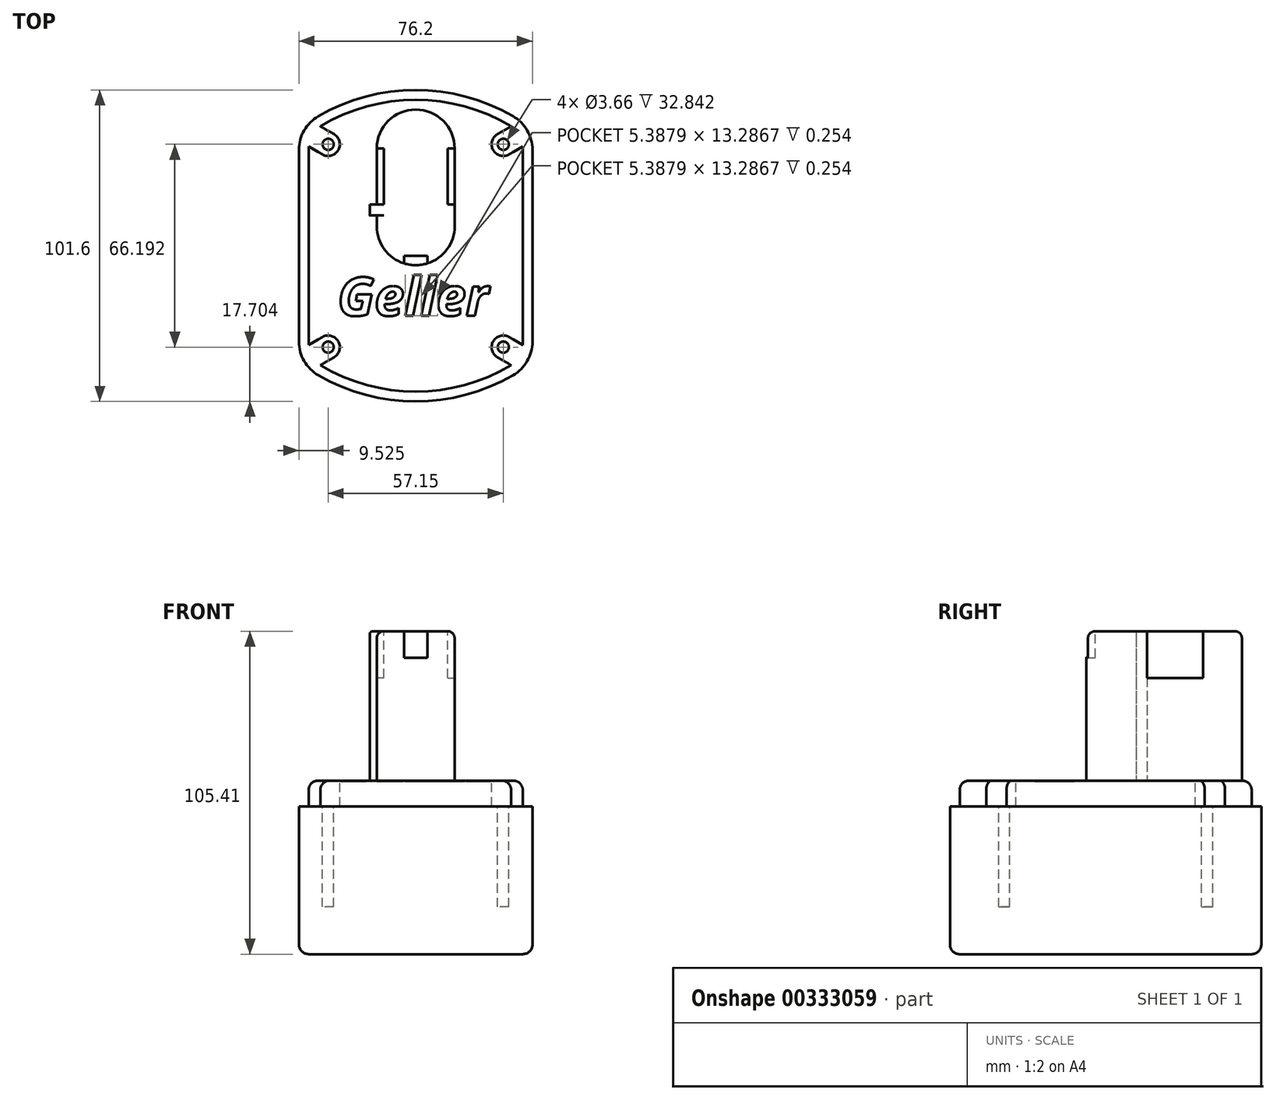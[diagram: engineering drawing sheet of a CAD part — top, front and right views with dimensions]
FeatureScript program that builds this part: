
annotation { "Feature Type Name" : "Feature", "Feature Type Description" : "" }
export const myFeature = defineFeature(function(context is Context, id is Id, definition is map)
    precondition{}
    {
        {
            var Q0;
            Q0=qCreatedBy(makeId("Top.planeOp"),FACE);
            var sketch = newSketch(context, id + "F0", { "sketchPlane" : qUnion([Q0])});
            skLineSegment(sketch, "E0.bottom", {"start": v(38.1, 38.1) * mm, "end": v(-38.1, 38.1) * mm, "construction": true});
            skLineSegment(sketch, "E0.top", {"start": v(38.1, -38.1) * mm, "end": v(-38.1, -38.1) * mm, "construction": true});
            skLineSegment(sketch, "E0.left", {"start": v(38.1, 38.1) * mm, "end": v(38.1, -38.1) * mm});
            skLineSegment(sketch, "E0.right", {"start": v(-38.1, 38.1) * mm, "end": v(-38.1, -38.1) * mm});
            skPoint(sketch, "E0.middle", {"position": v(0, 0) * mm});
            skLineSegment(sketch, "E1", {"start": v(0, 38.1) * mm, "end": v(0, 50.8) * mm, "construction": true});
            skPoint(sketch, "E1.endSnap0", {"position": v(0, 38.1) * mm});
            skArc(sketch, "E2", {"start": v(38.1, 38.1) * mm, "mid": v(0, 50.8) * mm, "end": v(-38.1, 38.1) * mm});
            skLineSegment(sketch, "E3", {"start": v(-38.1, 0) * mm, "end": v(38.1, 0) * mm, "construction": true});
            skArc(sketch, "E4.MirrorCS", {"start": v(38.1, -38.1) * mm, "mid": v(0, -50.8) * mm, "end": v(-38.1, -38.1) * mm});
            skSolve(sketch);
        }
        {
            var Q0;
            Q0 = qSketchRegion(id + "F0", true);
            extrude(context, id + "F1", {"entities" : qUnion([Q0]), "oppositeDirection" : true, "depth" : 48.26 * mm});
        }
        {
            var Q0;
            Q0=makeQuery(id+"F1.opExtrude","CAP_FACE",FACE,{"disambiguationData":[OSD([sQuery(id+"F0.wireOp",EDGE,"E0.left"),sQuery(id+"F0.wireOp",EDGE,"E0.right"),sQuery(id+"F0.wireOp",EDGE,"E2"),sQuery(id+"F0.wireOp",EDGE,"E4.MirrorCS")])],"isStart":true});
            var sketch = newSketch(context, id + "F2", { "sketchPlane" : qUnion([Q0])});
            skArc(sketch, "E5.0.0", {"start": v(38.1, 38.1) * mm, "mid": v(0, 50.8) * mm, "end": v(-38.1, 38.1) * mm, "construction": true});
            skLineSegment(sketch, "E5.0.1", {"start": v(-38.1, 38.1) * mm, "end": v(-38.1, -38.1) * mm, "construction": true});
            skArc(sketch, "E5.0.2", {"start": v(-38.1, -38.1) * mm, "mid": v(0, -50.8) * mm, "end": v(38.1, -38.1) * mm, "construction": true});
            skLineSegment(sketch, "E5.0.3", {"start": v(38.1, -38.1) * mm, "end": v(38.1, 38.1) * mm, "construction": true});
            skArc(sketch, "E6.0", {"start": v(34.93, 36.49) * mm, "mid": v(0, 47.63) * mm, "end": v(-34.93, 36.49) * mm});
            skLineSegment(sketch, "E6.1", {"start": v(34.93, -36.49) * mm, "end": v(34.93, 36.49) * mm});
            skArc(sketch, "E6.2", {"start": v(-34.93, -36.49) * mm, "mid": v(0, -47.63) * mm, "end": v(34.93, -36.49) * mm});
            skLineSegment(sketch, "E6.3", {"start": v(-34.93, 36.49) * mm, "end": v(-34.93, -36.49) * mm});
            skSolve(sketch);
        }
        {
            var Q0;
            Q0 = qSketchRegion(id + "F2", true);
            extrude(context, id + "F3", {"entities" : qUnion([Q0]), "operationType" : NewBodyOperationType.ADD, "depth" : 8.38 * mm});
        }
        {
            var Q0;
            Q0=makeQuery(id+"F3.opExtrude","CAP_FACE",FACE,{"disambiguationData":[OSD([sQuery(id+"F2.wireOp",EDGE,"E6.0"),sQuery(id+"F2.wireOp",EDGE,"E6.1"),sQuery(id+"F2.wireOp",EDGE,"E6.2"),sQuery(id+"F2.wireOp",EDGE,"E6.3")])],"isStart":false});
            var sketch = newSketch(context, id + "F4", { "sketchPlane" : qUnion([Q0])});
            skLineSegment(sketch, "E7.bottom", {"start": v(28.58, 33.1) * mm, "end": v(-28.58, 33.1) * mm, "construction": true});
            skLineSegment(sketch, "E7.top", {"start": v(28.57, -33.1) * mm, "end": v(-28.58, -33.1) * mm, "construction": true});
            skLineSegment(sketch, "E7.left", {"start": v(28.58, 33.1) * mm, "end": v(28.57, -33.1) * mm, "construction": true});
            skLineSegment(sketch, "E7.right", {"start": v(-28.58, 33.1) * mm, "end": v(-28.58, -33.1) * mm, "construction": true});
            skPoint(sketch, "E7.middle", {"position": v(0, 0) * mm});
            skLineSegment(sketch, "E8", {"start": v(-28.58, -33.1) * mm, "end": v(-50.57, -45.8) * mm, "construction": true});
            skArc(sketch, "E9.0.startCap", {"start": v(-30.48, -29.8) * mm, "mid": v(-25.28, -31.2) * mm, "end": v(-26.67, -36.4) * mm});
            skArc(sketch, "E9.0.endCap", {"start": v(-48.67, -49.1) * mm, "mid": v(-53.87, -47.7) * mm, "end": v(-52.48, -42.5) * mm});
            skLineSegment(sketch, "E9.0.left", {"start": v(-26.67, -36.4) * mm, "end": v(-48.67, -49.1) * mm});
            skLineSegment(sketch, "E9.0.right", {"start": v(-30.48, -29.8) * mm, "end": v(-52.48, -42.5) * mm});
            skLineSegment(sketch, "E10", {"start": v(-28.58, 0) * mm, "end": v(28.58, 0) * mm, "construction": true});
            skLineSegment(sketch, "E11", {"start": v(0, 33.1) * mm, "end": v(0, -33.1) * mm, "construction": true});
            skArc(sketch, "E12.MirrorCS", {"start": v(30.48, -29.8) * mm, "mid": v(25.28, -31.2) * mm, "end": v(26.67, -36.4) * mm});
            skLineSegment(sketch, "E13.MirrorCS", {"start": v(26.67, -36.4) * mm, "end": v(48.67, -49.1) * mm});
            skLineSegment(sketch, "E14.MirrorCS", {"start": v(30.48, -29.8) * mm, "end": v(52.48, -42.5) * mm});
            skArc(sketch, "E15.MirrorCS", {"start": v(48.67, -49.1) * mm, "mid": v(53.87, -47.7) * mm, "end": v(52.48, -42.5) * mm});
            skLineSegment(sketch, "E16.MirrorCS", {"start": v(30.48, 29.8) * mm, "end": v(52.48, 42.5) * mm});
            skLineSegment(sketch, "E17.MirrorCS", {"start": v(26.67, 36.4) * mm, "end": v(48.67, 49.1) * mm});
            skArc(sketch, "E18.MirrorCS", {"start": v(30.48, 29.8) * mm, "mid": v(25.28, 31.2) * mm, "end": v(26.67, 36.4) * mm});
            skArc(sketch, "E19.MirrorCS", {"start": v(48.67, 49.1) * mm, "mid": v(53.87, 47.7) * mm, "end": v(52.48, 42.5) * mm});
            skArc(sketch, "E20.MirrorCS", {"start": v(-30.48, 29.8) * mm, "mid": v(-25.28, 31.2) * mm, "end": v(-26.67, 36.4) * mm});
            skLineSegment(sketch, "E21.MirrorCS", {"start": v(-26.67, 36.4) * mm, "end": v(-48.67, 49.1) * mm});
            skLineSegment(sketch, "E22.MirrorCS", {"start": v(-30.48, 29.8) * mm, "end": v(-52.48, 42.5) * mm});
            skArc(sketch, "E23.MirrorCS", {"start": v(-48.67, 49.1) * mm, "mid": v(-53.87, 47.7) * mm, "end": v(-52.48, 42.5) * mm});
            skCircle(sketch, "E24", {"center": v(-28.58, 33.1) * mm, "radius": 1.83 * mm, "construction": true});
            skCircle(sketch, "E25", {"center": v(28.58, 33.1) * mm, "radius": 1.83 * mm, "construction": true});
            skCircle(sketch, "E26", {"center": v(-28.58, -33.1) * mm, "radius": 1.83 * mm, "construction": true});
            skCircle(sketch, "E27", {"center": v(28.57, -33.1) * mm, "radius": 1.83 * mm, "construction": true});
            skSolve(sketch);
        }
        {
            var Q0;
            Q0 = qSketchRegion(id + "F4", true);
            var Q1;
            Q1=makeQuery(id+"F1.opExtrude","CAP_FACE",FACE,{"disambiguationData":[OSD([sQuery(id+"F0.wireOp",EDGE,"E0.left"),sQuery(id+"F0.wireOp",EDGE,"E0.right"),sQuery(id+"F0.wireOp",EDGE,"E2"),sQuery(id+"F0.wireOp",EDGE,"E4.MirrorCS")])],"isStart":true});
            extrude(context, id + "F5", {"entities" : qUnion([Q0]), "operationType" : NewBodyOperationType.REMOVE, "endBound" : BoundingType.UP_TO_SURFACE, "oppositeDirection" : true, "endBoundEntityFace" : qUnion([Q1]), "depth" : 25.4 * mm});
        }
        {
            var Q0;
            Q0=makeQuery(id+"F2.imprint","IMPRINT",FACE,{"disambiguationData":[TD([[makeQuery(id+"F2.imprint","IMPRINT",EDGE,{"derivedFrom":sQuery(id+"F2.wireOp",EDGE,"E6.0")}),-1.0]])]});
            var sketch = newSketch(context, id + "F6", { "sketchPlane" : qUnion([Q0])});
            skCircle(sketch, "E28.0", {"center": v(-28.58, 33.1) * mm, "radius": 1.83 * mm});
            skCircle(sketch, "E28.1", {"center": v(28.58, 33.1) * mm, "radius": 1.83 * mm});
            skCircle(sketch, "E28.2", {"center": v(28.57, -33.1) * mm, "radius": 1.83 * mm});
            skCircle(sketch, "E28.3", {"center": v(-28.58, -33.1) * mm, "radius": 1.83 * mm});
            skSolve(sketch);
        }
        {
            var Q0;
            Q0 = qSketchRegion(id + "F6", true);
            extrude(context, id + "F7", {"entities" : qUnion([Q0]), "operationType" : NewBodyOperationType.REMOVE, "oppositeDirection" : true, "depth" : 32.84 * mm});
        }
        {
            var Q0;
            Q0=qCreatedBy(makeId("Top.planeOp"),FACE);
            var sketch = newSketch(context, id + "F8", { "sketchPlane" : qUnion([Q0])});
            skLineSegment(sketch, "E29", {"start": v(0, 6.35) * mm, "end": v(0, 31.75) * mm, "construction": true});
            skArc(sketch, "E30.0.startCap", {"start": v(12.7, 6.35) * mm, "mid": v(0, -6.35) * mm, "end": v(-12.7, 6.35) * mm});
            skArc(sketch, "E30.0.endCap", {"start": v(-12.7, 31.75) * mm, "mid": v(0, 44.45) * mm, "end": v(12.7, 31.75) * mm});
            skLineSegment(sketch, "E30.0.left", {"start": v(-12.7, 6.35) * mm, "end": v(-12.7, 31.75) * mm});
            skLineSegment(sketch, "E30.0.right", {"start": v(12.7, 6.35) * mm, "end": v(12.7, 31.75) * mm});
            skPoint(sketch, "E31", {"position": v(0, 19.05) * mm});
            skPoint(sketch, "E32", {"position": v(0, 44.45) * mm});
            skPoint(sketch, "E33", {"position": v(0, -6.35) * mm});
            skSolve(sketch);
        }
        {
            var Q0;
            Q0 = qSketchRegion(id + "F8", true);
            extrude(context, id + "F9", {"entities" : qUnion([Q0]), "operationType" : NewBodyOperationType.ADD, "depth" : 57.15 * mm});
        }
        {
            var Q0;
            Q0=makeQuery(id+"F3.opExtrude","CAP_FACE",FACE,{"disambiguationData":[OSD([sQuery(id+"F2.wireOp",EDGE,"E6.0"),sQuery(id+"F2.wireOp",EDGE,"E6.1"),sQuery(id+"F2.wireOp",EDGE,"E6.2"),sQuery(id+"F2.wireOp",EDGE,"E6.3")])],"isStart":false});
            var sketch = newSketch(context, id + "F10", { "sketchPlane" : qUnion([Q0])});
            skLineSegment(sketch, "E34.bottom", {"start": v(-12.7, 13.46) * mm, "end": v(-14.99, 13.46) * mm});
            skLineSegment(sketch, "E34.top", {"start": v(-12.7, 9.9) * mm, "end": v(-14.99, 9.9) * mm});
            skLineSegment(sketch, "E34.left", {"start": v(-12.7, 13.46) * mm, "end": v(-12.7, 9.9) * mm});
            skLineSegment(sketch, "E34.right", {"start": v(-14.99, 13.46) * mm, "end": v(-14.99, 9.9) * mm});
            skSolve(sketch);
        }
        {
            var Q0;
            Q0 = qSketchRegion(id + "F10", true);
            var Q1;
            Q1=makeQuery(id+"F9.opExtrude","CAP_FACE",FACE,{"disambiguationData":[OSD([sQuery(id+"F8.wireOp",EDGE,"E30.0.startCap"),sQuery(id+"F8.wireOp",EDGE,"E30.0.endCap"),sQuery(id+"F8.wireOp",EDGE,"E30.0.left"),sQuery(id+"F8.wireOp",EDGE,"E30.0.right")])],"isStart":false});
            extrude(context, id + "F11", {"entities" : qUnion([Q0]), "operationType" : NewBodyOperationType.ADD, "endBound" : BoundingType.UP_TO_SURFACE, "endBoundEntityFace" : qUnion([Q1]), "depth" : 25.4 * mm});
        }
        {
            var Q0;
            Q0=makeQuery(id+"F9.opExtrude","CAP_EDGE",EDGE,{"disambiguationData":[OSD([sQuery(id+"F8.wireOp",EDGE,"E30.0.right")])],"isStart":false});
            fillet(context, id + "F12", {"entities" : qUnion([Q0]), "radius" : 2.3 * mm, "tangentPropagation" : true, "allowEdgeOverflow" : false});
        }
        {
            var Q0;
            Q0=makeQuery(id+"F11.boolean.opBoolean","MERGE",FACE,{"derivedFrom":[makeQuery(id+"F9.opExtrude","CAP_FACE",FACE,{"disambiguationData":[OSD([sQuery(id+"F8.wireOp",EDGE,"E30.0.startCap"),sQuery(id+"F8.wireOp",EDGE,"E30.0.endCap"),sQuery(id+"F8.wireOp",EDGE,"E30.0.left"),sQuery(id+"F8.wireOp",EDGE,"E30.0.right")])],"isStart":false}),makeQuery(id+"F11.opExtrude","CAP_FACE",FACE,{"disambiguationData":[OSD([sQuery(id+"F10.wireOp",EDGE,"E34.bottom"),sQuery(id+"F10.wireOp",EDGE,"E34.top"),sQuery(id+"F10.wireOp",EDGE,"E34.left"),sQuery(id+"F10.wireOp",EDGE,"E34.right")])],"isStart":false})]});
            var sketch = newSketch(context, id + "F13", { "sketchPlane" : qUnion([Q0])});
            skLineSegment(sketch, "E35.bottom", {"start": v(10.41, 31.75) * mm, "end": v(12.7, 31.75) * mm});
            skLineSegment(sketch, "E35.top", {"start": v(10.41, 13.46) * mm, "end": v(12.7, 13.46) * mm});
            skLineSegment(sketch, "E35.left", {"start": v(10.41, 31.75) * mm, "end": v(10.41, 13.46) * mm});
            skLineSegment(sketch, "E35.right", {"start": v(12.7, 31.75) * mm, "end": v(12.7, 13.46) * mm});
            skLineSegment(sketch, "E36.0", {"start": v(0, 6.35) * mm, "end": v(0, 31.75) * mm, "construction": true});
            skLineSegment(sketch, "E37.MirrorCS", {"start": v(-10.41, 31.75) * mm, "end": v(-12.7, 31.75) * mm});
            skLineSegment(sketch, "E38.MirrorCS", {"start": v(-12.7, 31.75) * mm, "end": v(-12.7, 13.46) * mm});
            skLineSegment(sketch, "E39.MirrorCS", {"start": v(-10.41, 31.75) * mm, "end": v(-10.41, 13.46) * mm});
            skLineSegment(sketch, "E40.MirrorCS", {"start": v(-10.41, 13.46) * mm, "end": v(-12.7, 13.46) * mm});
            skArc(sketch, "E41.0", {"start": v(3.81, -5.77) * mm, "mid": v(0, -6.35) * mm, "end": v(-3.81, -5.77) * mm, "construction": true});
            skArc(sketch, "E41.1", {"start": v(-10.41, 6.35) * mm, "mid": v(0, -4.06) * mm, "end": v(10.41, 6.35) * mm, "construction": true});
            skLineSegment(sketch, "E42", {"start": v(-3.8, -5.77) * mm, "end": v(-3.8, -3.34) * mm, "construction": true});
            skLineSegment(sketch, "E43", {"start": v(-3.8, -3.34) * mm, "end": v(3.8, -3.34) * mm, "construction": true});
            skLineSegment(sketch, "E44", {"start": v(3.81, -3.34) * mm, "end": v(3.81, -5.77) * mm, "construction": true});
            skPoint(sketch, "E45.orphan", {"position": v(-12.7, 6.35) * mm});
            skPoint(sketch, "E46.orphan", {"position": v(12.7, 6.35) * mm});
            skSolve(sketch);
        }
        {
            var Q0;
            Q0 = qSketchRegion(id + "F13", true);
            extrude(context, id + "F14", {"entities" : qUnion([Q0]), "operationType" : NewBodyOperationType.REMOVE, "oppositeDirection" : true, "depth" : 15.24 * mm});
        }
        {
            var Q0;
            {var subQ7=sQuery(id+"F13.wireOp",EDGE,"E35.left");Q0=makeQuery(id+"F13.imprint","IMPRINT",FACE,{"disambiguationData":[TD([[makeQuery(id+"F13.imprint","IMPRINT",EDGE,{"derivedFrom":subQ7}),1.0]])]});}
            var sketch = newSketch(context, id + "F15", { "sketchPlane" : qUnion([Q0])});
            skLineSegment(sketch, "E47.0", {"start": v(-3.8, -5.77) * mm, "end": v(-3.8, -3.34) * mm});
            skLineSegment(sketch, "E47.1", {"start": v(-3.8, -3.34) * mm, "end": v(3.8, -3.34) * mm});
            skLineSegment(sketch, "E47.2", {"start": v(3.81, -3.34) * mm, "end": v(3.81, -5.77) * mm});
            skArc(sketch, "E48.0", {"start": v(3.8, -5.77) * mm, "mid": v(0, -6.35) * mm, "end": v(-3.81, -5.77) * mm});
            skPoint(sketch, "E49.orphan", {"position": v(-12.7, 6.35) * mm});
            skPoint(sketch, "E50.orphan", {"position": v(12.7, 6.35) * mm});
            skSolve(sketch);
        }
        {
            var Q0;
            Q0 = qSketchRegion(id + "F15", true);
            extrude(context, id + "F16", {"entities" : qUnion([Q0]), "operationType" : NewBodyOperationType.REMOVE, "oppositeDirection" : true, "depth" : 8.64 * mm});
        }
        {
            var Q0;
            Q0=makeQuery(id+"F11.opExtrude","CAP_EDGE",EDGE,{"disambiguationData":[OSD([sQuery(id+"F10.wireOp",EDGE,"E34.right")])],"isStart":false});
            fillet(context, id + "F17", {"entities" : qUnion([Q0]), "radius" : 1.02 * mm, "tangentPropagation" : true, "allowEdgeOverflow" : false});
        }
        {
            var Q0;
            Q0=makeQuery(id+"F3.opExtrude","CAP_FACE",FACE,{"disambiguationData":[OSD([sQuery(id+"F2.wireOp",EDGE,"E6.0"),sQuery(id+"F2.wireOp",EDGE,"E6.1"),sQuery(id+"F2.wireOp",EDGE,"E6.2"),sQuery(id+"F2.wireOp",EDGE,"E6.3")])],"isStart":false});
            var sketch = newSketch(context, id + "F18", { "sketchPlane" : qUnion([Q0])});
            skText(sketch, "E51", { "text": "Geller", "fontName": "OpenSans-BoldItalic.ttf"});
            skArc(sketch, "E52.0", {"start": v(-38.1, -38.1) * mm, "mid": v(0, -50.8) * mm, "end": v(38.1, -38.1) * mm});
            skLineSegment(sketch, "E53", {"start": v(0, -50.8) * mm, "end": v(0, -22.86) * mm, "construction": true});
            const initialGuessF18  = {"E51": [-0.02554, -0.02286, 1, 0, 0.01259]};
            skSetInitialGuess(sketch, initialGuessF18);
            skSolve(sketch);
        }
        {
            var Q0;
            Q0=makeQuery(id+"F18.imprint","IMPRINT",FACE,{"disambiguationData":[TD([[makeQuery(id+"F18.imprint","IMPRINT",EDGE,{"derivedFrom":sQuery(id+"F18.wireOp",EDGE,"E51.sketch_text.stroke-22")}),-1.0]])]});
            var Q1;
            Q1=makeQuery(id+"F18.imprint","IMPRINT",FACE,{"disambiguationData":[TD([[makeQuery(id+"F18.imprint","IMPRINT",EDGE,{"derivedFrom":sQuery(id+"F18.wireOp",EDGE,"E51.sketch_text.stroke-0")}),-1.0]])]});
            var Q2;
            Q2=makeQuery(id+"F18.imprint","IMPRINT",FACE,{"disambiguationData":[TD([[makeQuery(id+"F18.imprint","IMPRINT",EDGE,{"derivedFrom":sQuery(id+"F18.wireOp",EDGE,"E51.sketch_text.stroke-46")}),-1.0]])]});
            var Q3;
            Q3=makeQuery(id+"F18.imprint","IMPRINT",FACE,{"disambiguationData":[TD([[makeQuery(id+"F18.imprint","IMPRINT",EDGE,{"derivedFrom":sQuery(id+"F18.wireOp",EDGE,"E51.sketch_text.stroke-50")}),-1.0]])]});
            var Q4;
            Q4=makeQuery(id+"F18.imprint","IMPRINT",FACE,{"disambiguationData":[TD([[makeQuery(id+"F18.imprint","IMPRINT",EDGE,{"derivedFrom":sQuery(id+"F18.wireOp",EDGE,"E51.sketch_text.stroke-54")}),-1.0]])]});
            var Q5;
            Q5=makeQuery(id+"F18.imprint","IMPRINT",FACE,{"disambiguationData":[TD([[makeQuery(id+"F18.imprint","IMPRINT",EDGE,{"derivedFrom":sQuery(id+"F18.wireOp",EDGE,"E51.sketch_text.stroke-78")}),-1.0]])]});
            extrude(context, id + "F19", {"entities" : qUnion([Q0, Q1, Q2, Q3, Q4, Q5]), "operationType" : NewBodyOperationType.REMOVE, "oppositeDirection" : true, "depth" : 0.25 * mm});
        }
        {
            var Q0;
            Q0=makeQuery(id+"F1.opExtrude","SWEPT_EDGE",EDGE,{"disambiguationData":[OSD([sQuery(id+"F0.wireOp",EDGE,"E0.left"),sQuery(id+"F0.wireOp",EDGE,"E4.MirrorCS")])]});
            var Q1;
            Q1=makeQuery(id+"F1.opExtrude","SWEPT_EDGE",EDGE,{"disambiguationData":[OSD([sQuery(id+"F0.wireOp",EDGE,"E0.left"),sQuery(id+"F0.wireOp",EDGE,"E2")])]});
            var Q2;
            Q2=makeQuery(id+"F1.opExtrude","SWEPT_EDGE",EDGE,{"disambiguationData":[OSD([sQuery(id+"F0.wireOp",EDGE,"E0.right"),sQuery(id+"F0.wireOp",EDGE,"E4.MirrorCS")])]});
            var Q3;
            Q3=makeQuery(id+"F1.opExtrude","SWEPT_EDGE",EDGE,{"disambiguationData":[OSD([sQuery(id+"F0.wireOp",EDGE,"E0.right"),sQuery(id+"F0.wireOp",EDGE,"E2")])]});
            fillet(context, id + "F20", {"entities" : qUnion([Q0, Q1, Q2, Q3]), "radius" : 12.7 * mm, "tangentPropagation" : true, "allowEdgeOverflow" : false});
        }
        {
            var Q0;
            Q0=makeQuery(id+"F3.opExtrude","CAP_EDGE",EDGE,{"disambiguationData":[OSD([sQuery(id+"F2.wireOp",EDGE,"E6.2")])],"isStart":false});
            var Q1;
            Q1=makeQuery(id+"F3.opExtrude","CAP_EDGE",EDGE,{"disambiguationData":[OSD([sQuery(id+"F2.wireOp",EDGE,"E6.1")])],"isStart":false});
            var Q2;
            Q2=makeQuery(id+"F3.opExtrude","CAP_EDGE",EDGE,{"disambiguationData":[OSD([sQuery(id+"F2.wireOp",EDGE,"E6.3")])],"isStart":false});
            var Q3;
            Q3=makeQuery(id+"F3.opExtrude","CAP_EDGE",EDGE,{"disambiguationData":[OSD([sQuery(id+"F2.wireOp",EDGE,"E6.0")])],"isStart":false});
            fillet(context, id + "F21", {"entities" : qUnion([Q0, Q1, Q2, Q3]), "radius" : 3.05 * mm, "tangentPropagation" : true, "allowEdgeOverflow" : false});
        }
        {
            var Q0;
            Q0=makeQuery(id+"F1.opExtrude","CAP_EDGE",EDGE,{"disambiguationData":[OSD([sQuery(id+"F0.wireOp",EDGE,"E0.left")])],"isStart":false});
            fillet(context, id + "F22", {"entities" : qUnion([Q0]), "radius" : 3.17 * mm, "tangentPropagation" : true, "allowEdgeOverflow" : false});
        }
    });
